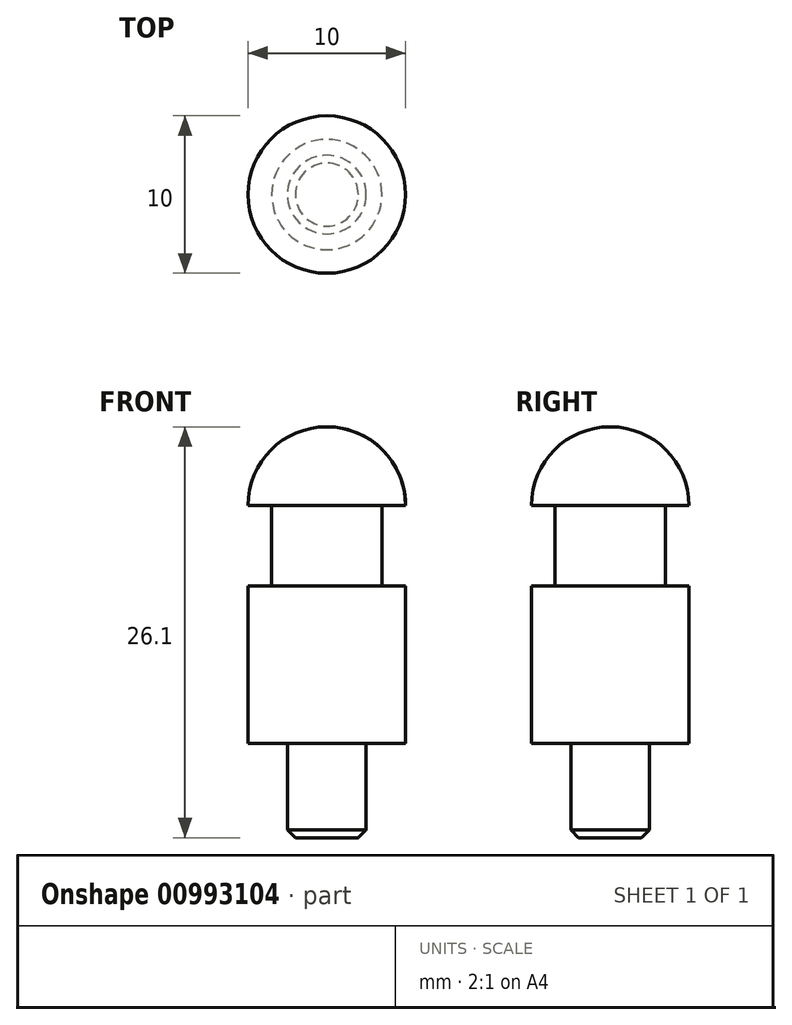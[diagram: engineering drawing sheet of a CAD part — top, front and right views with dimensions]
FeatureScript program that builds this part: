
annotation { "Feature Type Name" : "Feature", "Feature Type Description" : "" }
export const myFeature = defineFeature(function(context is Context, id is Id, definition is map)
    precondition{}
    {
        {
            var Q0;
            Q0=qCreatedBy(makeId("Top.planeOp"),FACE);
            var sketch = newSketch(context, id + "F0", { "sketchPlane" : qUnion([Q0])});
            skCircle(sketch, "E0", {"center": v(0, 0) * mm, "radius": 2.5 * mm});
            skSolve(sketch);
        }
        {
            var Q0;
            Q0=qSketchRegion(id+"F0",true);
            extrude(context, id + "F1", {"entities" : qUnion([Q0]), "depth" : 6 * mm});
        }
        {
            var Q0;
            Q0=makeQuery(id+"F1.opExtrude","CAP_FACE",FACE,{"disambiguationData":[OSD([sQuery(id+"F0.wireOp",EDGE,"E0")])],"isStart":false});
            var sketch = newSketch(context, id + "F2", { "sketchPlane" : qUnion([Q0])});
            skCircle(sketch, "E1", {"center": v(0, 0) * mm, "radius": 5 * mm});
            skSolve(sketch);
        }
        {
            var Q0;
            Q0=qSketchRegion(id+"F2",true);
            extrude(context, id + "F3", {"entities" : qUnion([Q0]), "operationType" : NewBodyOperationType.ADD, "depth" : 10 * mm});
        }
        {
            var Q0;
            Q0=makeQuery(id+"F3.opExtrude","CAP_FACE",FACE,{"disambiguationData":[OSD([sQuery(id+"F2.wireOp",EDGE,"E1")])],"isStart":false});
            var sketch = newSketch(context, id + "F4", { "sketchPlane" : qUnion([Q0])});
            skCircle(sketch, "E2", {"center": v(0, 0) * mm, "radius": 3.5 * mm});
            skSolve(sketch);
        }
        {
            var Q0;
            Q0=qSketchRegion(id+"F4",true);
            extrude(context, id + "F5", {"entities" : qUnion([Q0]), "operationType" : NewBodyOperationType.ADD, "depth" : 5.1 * mm});
        }
        {
            var Q0;
            Q0=makeQuery(id+"F5.opExtrude","CAP_FACE",FACE,{"disambiguationData":[OSD([sQuery(id+"F4.wireOp",EDGE,"E2")])],"isStart":false});
            var sketch = newSketch(context, id + "F6", { "sketchPlane" : qUnion([Q0])});
            skCircle(sketch, "E3", {"center": v(0, 0) * mm, "radius": 5 * mm});
            skSolve(sketch);
        }
        {
            var Q0;
            Q0=qSketchRegion(id+"F6",true);
            extrude(context, id + "F7", {"entities" : qUnion([Q0]), "operationType" : NewBodyOperationType.ADD, "depth" : 5 * mm});
        }
        {
            var Q0;
            Q0=makeQuery(id+"F1.opExtrude","CAP_EDGE",EDGE,{"disambiguationData":[OSD([sQuery(id+"F0.wireOp",EDGE,"E0")])],"isStart":true});
            chamfer(context, id + "F8", {"entities" : qUnion([Q0]), "width" : 0.5 * mm, "tangentPropagation" : true});
        }
        {
            var Q0;
            Q0=makeQuery(id+"F7.opExtrude","CAP_EDGE",EDGE,{"disambiguationData":[OSD([sQuery(id+"F6.wireOp",EDGE,"E3")])],"isStart":false});
            fillet(context, id + "F9", {"entities" : qUnion([Q0]), "radius" : 5 * mm, "tangentPropagation" : true, "allowEdgeOverflow" : false});
        }
    });
